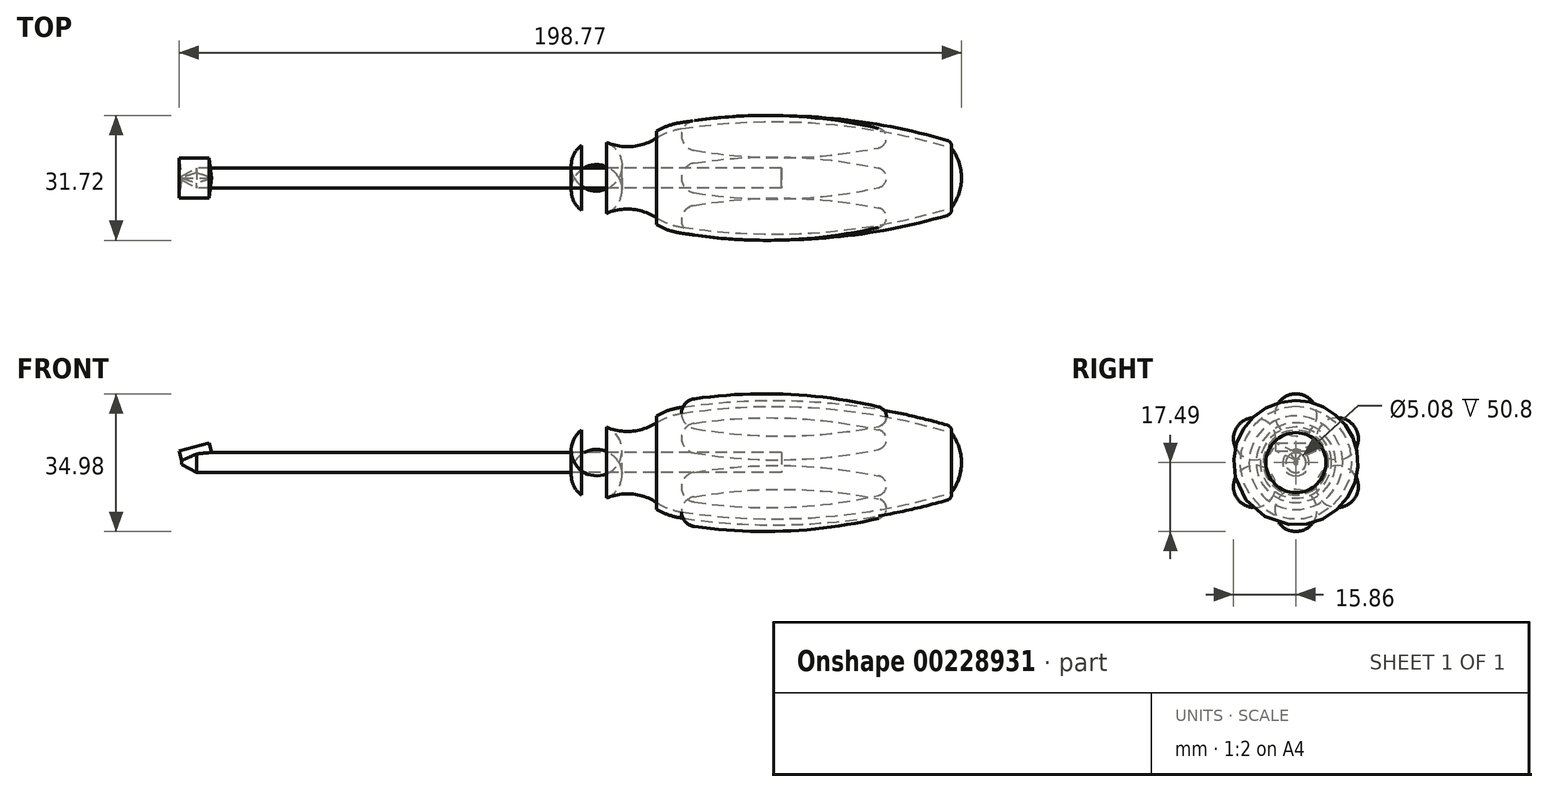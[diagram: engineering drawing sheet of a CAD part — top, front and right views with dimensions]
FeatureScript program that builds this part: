
annotation { "Feature Type Name" : "Feature", "Feature Type Description" : "" }
export const myFeature = defineFeature(function(context is Context, id is Id, definition is map)
    precondition{}
    {
        {
            var Q0;
            Q0=qCreatedBy(makeId("Front.planeOp"),FACE);
            var sketch = newSketch(context, id + "F0", { "sketchPlane" : qUnion([Q0])});
            skLineSegment(sketch, "E0", {"start": v(-101.6, 0) * mm, "end": v(96.52, 0) * mm});
            skLineSegment(sketch, "E1", {"start": v(96.52, 0) * mm, "end": v(117.55, 0) * mm, "construction": true});
            skLineSegment(sketch, "E2", {"start": v(50.8, 2.54) * mm, "end": v(-97.8, 2.54) * mm});
            skLineSegment(sketch, "E3", {"start": v(-101.6, 0.5) * mm, "end": v(-101.6, 0) * mm});
            skLineSegment(sketch, "E4", {"start": v(0, 2.54) * mm, "end": v(0, 8.25) * mm});
            skArc(sketch, "E5", {"start": v(6.35, 9.02) * mm, "mid": v(3.07, 9.48) * mm, "end": v(0, 8.25) * mm});
            skArc(sketch, "E6", {"start": v(6.35, 9.02) * mm, "mid": v(12.84, 7.99) * mm, "end": v(19.05, 10.11) * mm});
            skArc(sketch, "E7", {"start": v(25.4, 12.52) * mm, "mid": v(22.1, 11.65) * mm, "end": v(19.05, 10.11) * mm});
            skArc(sketch, "E8", {"start": v(93.98, 7.62) * mm, "mid": v(59.96, 13.9) * mm, "end": v(25.4, 12.52) * mm});
            skArc(sketch, "E9", {"start": v(96.52, 0) * mm, "mid": v(95.87, 4.02) * mm, "end": v(93.98, 7.62) * mm});
            skArc(sketch, "E10.0", {"start": v(25.17, 14.02) * mm, "mid": v(22.01, 13.24) * mm, "end": v(19.05, 11.9) * mm});
            skArc(sketch, "E10.1", {"start": v(92.95, 9.52) * mm, "mid": v(59.3, 15.46) * mm, "end": v(25.17, 14.02) * mm});
            skLineSegment(sketch, "E11", {"start": v(19.05, 11.9) * mm, "end": v(19.05, 10.11) * mm});
            skArc(sketch, "E12", {"start": v(93.98, 7.62) * mm, "mid": v(93.86, 8.78) * mm, "end": v(92.95, 9.52) * mm});
            skPoint(sketch, "E13.orphan", {"position": v(0, 0) * mm});
            skLineSegment(sketch, "E14", {"start": v(50.8, 2.54) * mm, "end": v(50.8, 0) * mm});
            skLineSegment(sketch, "E15", {"start": v(-101.6, 0.5) * mm, "end": v(-97.8, 2.54) * mm});
            skPoint(sketch, "E16.orphan", {"position": v(-101.6, 2.54) * mm});
            skSolve(sketch);
        }
        {
            var Q0;
            Q0=qCreatedBy(makeId("Front.planeOp"),FACE);
            var sketch = newSketch(context, id + "F1", { "sketchPlane" : qUnion([Q0])});
            skLineSegment(sketch, "E17", {"start": v(25.4, 12.52) * mm, "end": v(77.47, 11.64) * mm});
            skArc(sketch, "E18", {"start": v(28.67, 16.22) * mm, "mid": v(26.35, 14.97) * mm, "end": v(25.4, 12.52) * mm});
            skArc(sketch, "E19", {"start": v(77.47, 11.64) * mm, "mid": v(76.93, 13.25) * mm, "end": v(75.5, 14.16) * mm});
            skArc(sketch, "E20", {"start": v(75.5, 14.16) * mm, "mid": v(52.19, 17.37) * mm, "end": v(28.67, 16.22) * mm});
            skSolve(sketch);
        }
        {
            var Q0;
            Q0=qCreatedBy(makeId("Front.planeOp"),FACE);
            var sketch = newSketch(context, id + "F2", { "sketchPlane" : qUnion([Q0])});
            skLineSegment(sketch, "E21", {"start": v(-101.6, 0.5) * mm, "end": v(-93.98, 2.54) * mm});
            skSolve(sketch);
        }
        {
            var Q0;
            Q0=sQuery(id+"F2.wireOp",VERTEX,"E21.start");
            var Q1;
            Q1=sQuery(id+"F2.wireOp",EDGE,"E21");
            cPlane(context, id + "F3", {"entities" : qUnion([Q0, Q1]), "cplaneType" : CPlaneType.LINE_POINT, "offset" : 25.4 * mm, "width" : 152.4 * mm, "height" : 152.4 * mm});
        }
        {
            var Q0;
            Q0=qCreatedBy(id+"F3.planeOp",FACE);
            var sketch = newSketch(context, id + "F4", { "sketchPlane" : qUnion([Q0])});
            skLineSegment(sketch, "E22", {"start": v(5.08, 29.2) * mm, "end": v(0, 26.67) * mm});
            skLineSegment(sketch, "E23", {"start": v(0, 26.67) * mm, "end": v(-5.08, 29.2) * mm});
            skLineSegment(sketch, "E24", {"start": v(-5.08, 29.2) * mm, "end": v(5.08, 29.2) * mm});
            skLineSegment(sketch, "E25", {"start": v(0, 29.2) * mm, "end": v(0, 26.67) * mm, "construction": true});
            skSolve(sketch);
        }
        {
            var Q0;
            {var subQ0=sQuery(id+"F0.wireOp",EDGE,"E3");Q0=makeQuery(id+"F0.imprint","IMPRINT",FACE,{"disambiguationData":[TD([[makeQuery(id+"F0.imprint","IMPRINT",EDGE,{"derivedFrom":subQ0}),1.0]])]});}
            var Q1;
            Q1=sQuery(id+"F0.wireOp",EDGE,"E1");
            revolve(context, id + "F5", {"entities" : qUnion([Q0]), "axis" : qUnion([Q1]), "revolveType" : RevolveType.FULL});
        }
        {
            var Q0;
            {var subQ0=sQuery(id+"F0.wireOp",EDGE,"E4");Q0=makeQuery(id+"F0.imprint","IMPRINT",FACE,{"disambiguationData":[TD([[makeQuery(id+"F0.imprint","IMPRINT",EDGE,{"derivedFrom":subQ0}),-1.0]])]});}
            var Q1;
            Q1=sQuery(id+"F0.wireOp",EDGE,"E1");
            revolve(context, id + "F6", {"entities" : qUnion([Q0]), "axis" : qUnion([Q1]), "revolveType" : RevolveType.FULL});
        }
        {
            var Q0;
            Q0=makeQuery(id+"F0.imprint","IMPRINT",FACE,{"disambiguationData":[TD([[makeQuery(id+"F0.imprint","IMPRINT",EDGE,{"derivedFrom":sQuery(id+"F0.wireOp",EDGE,"E7")}),-1.0]])]});
            var Q1;
            Q1=sQuery(id+"F0.wireOp",EDGE,"E1");
            revolve(context, id + "F7", {"entities" : qUnion([Q0]), "axis" : qUnion([Q1]), "revolveType" : RevolveType.FULL});
        }
        {
            var Q0;
            Q0=makeQuery(id+"F1.imprint","IMPRINT",FACE,{"disambiguationData":[TD([[makeQuery(id+"F1.imprint","IMPRINT",EDGE,{"derivedFrom":sQuery(id+"F1.wireOp",EDGE,"E17")}),1.0]])]});
            var Q1;
            Q1=sQuery(id+"F1.wireOp",EDGE,"E17");
            revolve(context, id + "F8", {"entities" : qUnion([Q0]), "axis" : qUnion([Q1]), "revolveType" : RevolveType.FULL});
        }
        {
            var Q0;
            Q0=makeQuery(id+"F8.opRevolve","SWEPT_BODY",BODY,{"disambiguationData":[OSD([sQuery(id+"F1.wireOp",EDGE,"E17"),sQuery(id+"F1.wireOp",EDGE,"E18"),sQuery(id+"F1.wireOp",EDGE,"E19"),sQuery(id+"F1.wireOp",EDGE,"E20")])]});
            var Q1;
            Q1=sQuery(id+"F0.wireOp",EDGE,"E1");
            circularPattern(context, id + "F9", {"entities" : qUnion([Q0]), "axis" : qUnion([Q1]), "angle" : 360 * degree, "instanceCount" : 6, "equalSpace" : true});
        }
        {
            var Q0;
            Q0=makeQuery(id+"F6.opRevolve","SWEPT_BODY",BODY,{"disambiguationData":[OSD([sQuery(id+"F0.wireOp",EDGE,"E0"),sQuery(id+"F0.wireOp",EDGE,"E2"),sQuery(id+"F0.wireOp",EDGE,"E4"),sQuery(id+"F0.wireOp",EDGE,"E5"),sQuery(id+"F0.wireOp",EDGE,"E6"),sQuery(id+"F0.wireOp",EDGE,"E7"),sQuery(id+"F0.wireOp",EDGE,"E8"),sQuery(id+"F0.wireOp",EDGE,"E9"),sQuery(id+"F0.wireOp",EDGE,"E14")])]});
            var Q1;
            Q1=makeQuery(id+"F7.opRevolve","SWEPT_BODY",BODY,{"disambiguationData":[OSD([sQuery(id+"F0.wireOp",EDGE,"E7"),sQuery(id+"F0.wireOp",EDGE,"E8"),sQuery(id+"F0.wireOp",EDGE,"E10.0"),sQuery(id+"F0.wireOp",EDGE,"E10.1"),sQuery(id+"F0.wireOp",EDGE,"E11"),sQuery(id+"F0.wireOp",EDGE,"E12")])]});
            booleanBodies(context, id + "F10", {"operationType" : BooleanOperationType.SUBTRACTION, "tools" : qUnion([Q0]), "targets" : qUnion([Q1]), "keepTools" : true});
        }
        {
            var Q0;
            Q0=makeQuery(id+"F4.imprint","IMPRINT",FACE,{"disambiguationData":[TD([[makeQuery(id+"F4.imprint","IMPRINT",EDGE,{"derivedFrom":sQuery(id+"F4.wireOp",EDGE,"E22")}),-1.0]])]});
            var Q1;
            Q1=sQuery(id+"F2.wireOp",EDGE,"E21");
            sweep(context, id + "F11", {"operationType" : NewBodyOperationType.REMOVE, "profiles" : qUnion([Q0]), "path" : qUnion([Q1])});
        }
        {
            var Q0;
            Q0=makeQuery(id+"F4.imprint","IMPRINT",FACE,{"disambiguationData":[TD([[makeQuery(id+"F4.imprint","IMPRINT",EDGE,{"derivedFrom":sQuery(id+"F4.wireOp",EDGE,"E22")}),-1.0]])]});
            var Q1;
            Q1=qConstructionFilter(qBodyType(qCreatedBy(id+"F2",EDGE),BodyType.WIRE),ConstructionObject.NO);
            sweep(context, id + "F12", {"profiles" : qUnion([Q0]), "path" : qUnion([Q1])});
        }
    });
